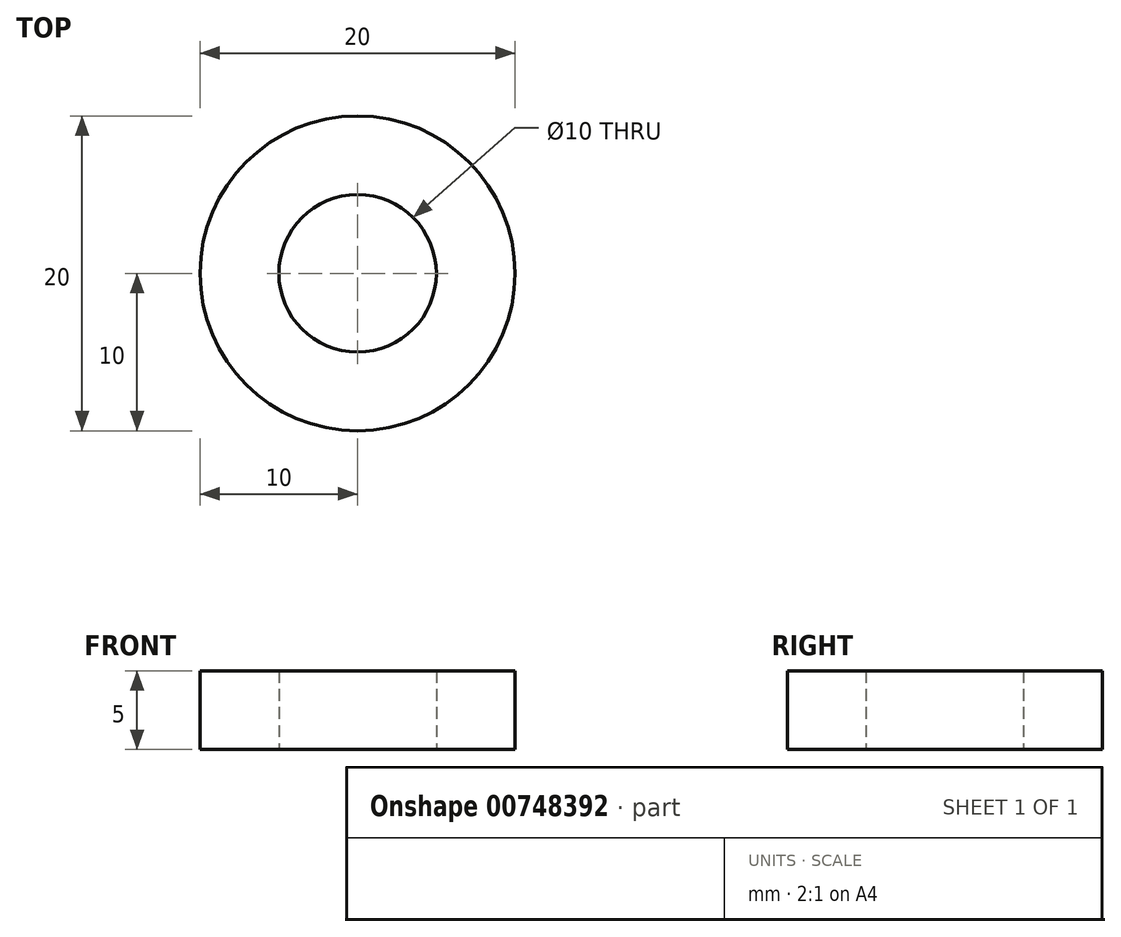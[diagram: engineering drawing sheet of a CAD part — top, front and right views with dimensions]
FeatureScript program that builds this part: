
annotation { "Feature Type Name" : "Feature", "Feature Type Description" : "" }
export const myFeature = defineFeature(function(context is Context, id is Id, definition is map)
    precondition{}
    {
        {
            var Q0;
            Q0=qCreatedBy(makeId("Top.planeOp"),FACE);
            var sketch = newSketch(context, id + "F0", { "sketchPlane" : qUnion([Q0])});
            skCircle(sketch, "E0", {"center": v(0, 0) * mm, "radius": 10 * mm});
            skCircle(sketch, "E1", {"center": v(0, 0) * mm, "radius": 5 * mm});
            skSolve(sketch);
        }
        {
            var Q0;
            Q0=makeQuery(id+"F0.imprint","IMPRINT",FACE,{"disambiguationData":[TD([[makeQuery(id+"F0.imprint","IMPRINT",EDGE,{"derivedFrom":sQuery(id+"F0.wireOp",EDGE,"E0")}),1.0]])]});
            extrude(context, id + "F1", {"entities" : qUnion([Q0]), "depth" : 5 * mm, "offsetDistance" : 25 * mm});
        }
    });
